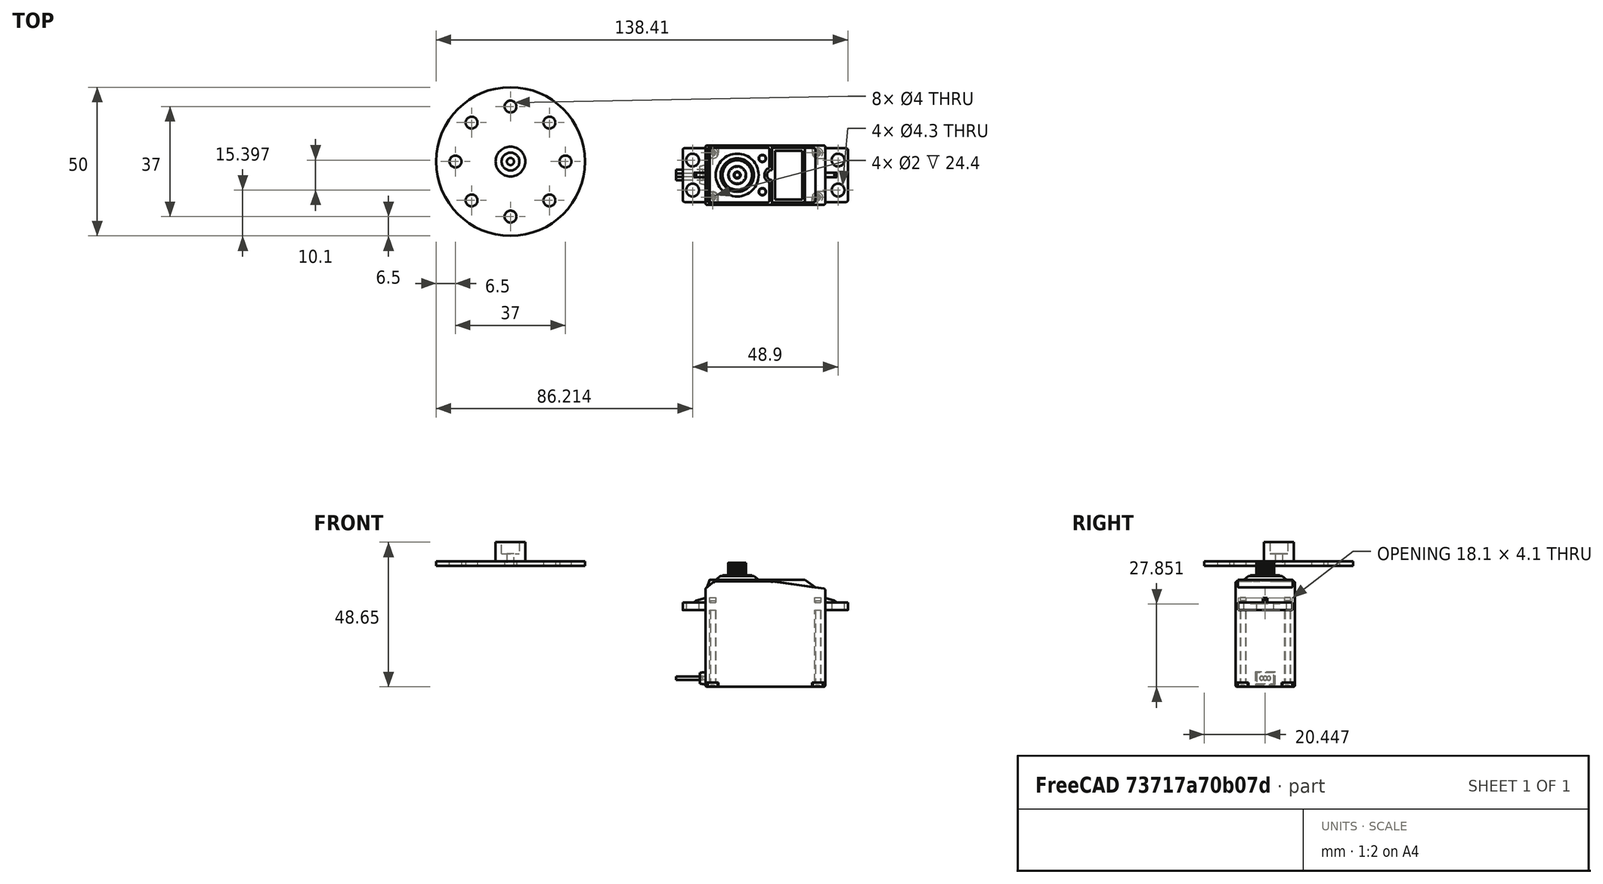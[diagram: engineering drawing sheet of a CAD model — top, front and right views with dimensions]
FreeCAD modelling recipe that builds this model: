
FCSTD DOCUMENT  (FreeCAD 0.21R33694 (Git))
Label: rotor_v3
License: All rights reserved
LicenseURL: http://en.wikipedia.org/wiki/All_rights_reserved
objects: Part::Cylinder×11, Part::MultiFuse×3, Part::Feature×1, Sketcher::SketchObject×1, Part::Extrusion×1, Part::Cut×1
note: 18 computed .brp shape members not serialized (recipe doc carries the construction recipe); baked Part::Feature solids carry a one-line shape summary decoded from their .brp

FEATURE [Part::Cylinder] cylinder
  Angle = 360
  AttacherType = Attacher::AttachEngine3D
  FirstAngle = 0
  Height = 1.5
  Radius = 25
  SecondAngle = 0
FEATURE [Part::Cylinder] cylinder002
  Angle = 360
  AttacherType = Attacher::AttachEngine3D
  FirstAngle = 0
  Height = 5
  Placement = pos=(18.5,0,0) rot=(0,0,1;0rad)
  Radius = 2
  SecondAngle = 0
FEATURE [Part::Cylinder] cylinder003
  Angle = 360
  AttacherType = Attacher::AttachEngine3D
  FirstAngle = 0
  Height = 5
  Placement = pos=(13.0815,13.0815,0) rot=(0,0,1;0.785398rad)
  Radius = 2
  SecondAngle = 0
FEATURE [Part::Cylinder] cylinder004
  Angle = 360
  AttacherType = Attacher::AttachEngine3D
  FirstAngle = 0
  Height = 5
  Placement = pos=(0,18.5,0) rot=(0,0,1;1.5708rad)
  Radius = 2
  SecondAngle = 0
FEATURE [Part::Cylinder] cylinder005
  Angle = 360
  AttacherType = Attacher::AttachEngine3D
  FirstAngle = 0
  Height = 5
  Placement = pos=(-13.0815,13.0815,0) rot=(0,0,1;2.35619rad)
  Radius = 2
  SecondAngle = 0
FEATURE [Part::Cylinder] cylinder006
  Angle = 360
  AttacherType = Attacher::AttachEngine3D
  FirstAngle = 0
  Height = 5
  Placement = pos=(-18.5,2e-15,0) rot=(0,0,1;3.14159rad)
  Radius = 2
  SecondAngle = 0
FEATURE [Part::Cylinder] cylinder007
  Angle = 360
  AttacherType = Attacher::AttachEngine3D
  FirstAngle = 0
  Height = 5
  Placement = pos=(-13.0815,-13.0815,0) rot=(0,0,1;3.92699rad)
  Radius = 2
  SecondAngle = 0
FEATURE [Part::Cylinder] cylinder008
  Angle = 360
  AttacherType = Attacher::AttachEngine3D
  FirstAngle = 0
  Height = 5
  Placement = pos=(0,-18.5,0) rot=(0,0,-1;1.5708rad)
  Radius = 2
  SecondAngle = 0
FEATURE [Part::Cylinder] cylinder009
  Angle = 360
  AttacherType = Attacher::AttachEngine3D
  FirstAngle = 0
  Height = 5
  Placement = pos=(13.0815,-13.0815,0) rot=(0,0,-1;0.785398rad)
  Radius = 2
  SecondAngle = 0
FEATURE [Part::MultiFuse] Group
  Placement = pos=(0,0,-1) rot=(0,0,1;0rad)
  Shapes = -> [cylinder002,cylinder003,cylinder004,cylinder005,cylinder006,cylinder007,cylinder008,cylinder009]
FEATURE [Part::Feature] Shape001
  Placement = pos=(85.6641,-4.55315,-40.6487) rot=(0,0,1;3.14159rad)
  shape: bbox 57.75 x 20 x 41.74 mm, 378 faces, 4 solids (baked)
FEATURE [Part::Cylinder] cylinder010  label="servo_central_shaft"
  Angle = 360
  AttacherType = Attacher::AttachEngine3D
  FirstAngle = 0
  Height = 8
  Radius = 5
  SecondAngle = 0
FEATURE [Sketcher::SketchObject] Sketch
  FullyConstrained = false
  MapMode = 5
  Placement = pos=(85.6641,-4.55315,1.09128) rot=(0,0,1;3.14159rad)
  Support = -> [Shape001]
  sketch-geometry (1):
    g0: Circle CenterX=9.4502 CenterY=-0.000218 CenterZ=0 NormalX=0 NormalY=0 NormalZ=1 AngleXU=0 Radius=3
  constraints (1):
    c: Radius(g0) = 3
FEATURE [Part::Extrusion] Extrude
  Base = -> Sketch
  Dir = (0,0,1)
  DirMode = 2
  FaceMakerClass = Part::FaceMakerBullseye
  LengthFwd = 6
  LengthRev = 0
  Placement = pos=(-76.21,4.55,3) rot=(0,0,1;0rad)
  Solid = true
  Symmetric = false
FEATURE [Part::Cylinder] Cylinder
  Angle = 360
  AttacherType = Attacher::AttachEngine3D
  FirstAngle = 0
  Height = 19
  Placement = pos=(0,0,-1) rot=(0,0,1;0rad)
  Radius = 1.2
  SecondAngle = 0
FEATURE [Part::MultiFuse] Fusion
  Shapes = -> [Group,Extrude,Cylinder]
FEATURE [Part::MultiFuse] Fusion001
  Shapes = -> [cylinder,cylinder010]
FEATURE [Part::Cut] Cut  label="rotor"
  Base = -> Fusion001
  Tool = -> Fusion
